# Revit family: Gira_541500
name_source: partatom
category: Allgemeines Modell
revit_build: Autodesk Revit 2017 (Build: 20160225_1515(x64)
units: mm (PartAtom-declared; Revit-internal decimal feet)

## family parameters
Basisbauteil = Fläche
Beim Laden mit Abzugskörper schneiden = Nein
Bemaßung runder Anschluss = Durchmesser verwenden
Gemeinsam genutzt = Nein
Kann Basisbauteil für Bewehrung sein = Nein
Raumberechnungspunkt = Nein
Teiletyp = Normal

## types (1)
- Gira_541500
    Assembly arrangement = Basic element
    BIM = https://media.stage.bim.site
    Beschreibung = S3000 blind ctrl.-w o aux.in Ins.,System 3000 blind controller insert without auxiliary input,,,Features:,- Control of electrically operated blinds, shutters and awnings.,- An individual intermediate position can be saved together with a top unit.,- Controlling a motor, e.g. to set the end positions, can be done without a top unit.,- Polarity reversal function for the outputs for simplified commissioning as of index I01.,- Operation with neutral conductor connection.
    Colour = Other
    Data sheet = https://katalog.gira.de
    GTIN = 4010337027416
    HAN = 541500
    Halogen free = Nein
    Hersteller = Gira
    Integrated timer = Nein
    Material = Other
    Material quality = Other
    Max. switching power [Voltampere] = 1000
    Mounting method = Flush mounted (plaster)
    Nominal voltage [Volt] = 230
    Productwebsite = http://katalog.gira.de
    Random generator = Nein
    Substation input = Nein
    Suitable for degree of protection (IP) = IP20
    Suitable for rain sensor = Nein
    Suitable for wind sensor = Nein
    Surface finishing = Not applicable
    Surface protection = Other
    Switch-off protection = Nein
    Transparent = Nein
    Type of fastening = Mounting with claw and screw
    Typname = S3000 blind ctrl.ins. w/o aux.inputs Insert
    URL = https://www.gira.de
    Vorgabe-Ansicht = 1219 mm
    With Astro program = Nein
    With brightness sensor connection = Nein
    With glass breaking detector connection = Nein
    With memory function = Nein

## geometry (parser evidence)
native form markers: Sweep x2
no freeform markers — native parametric forms only
